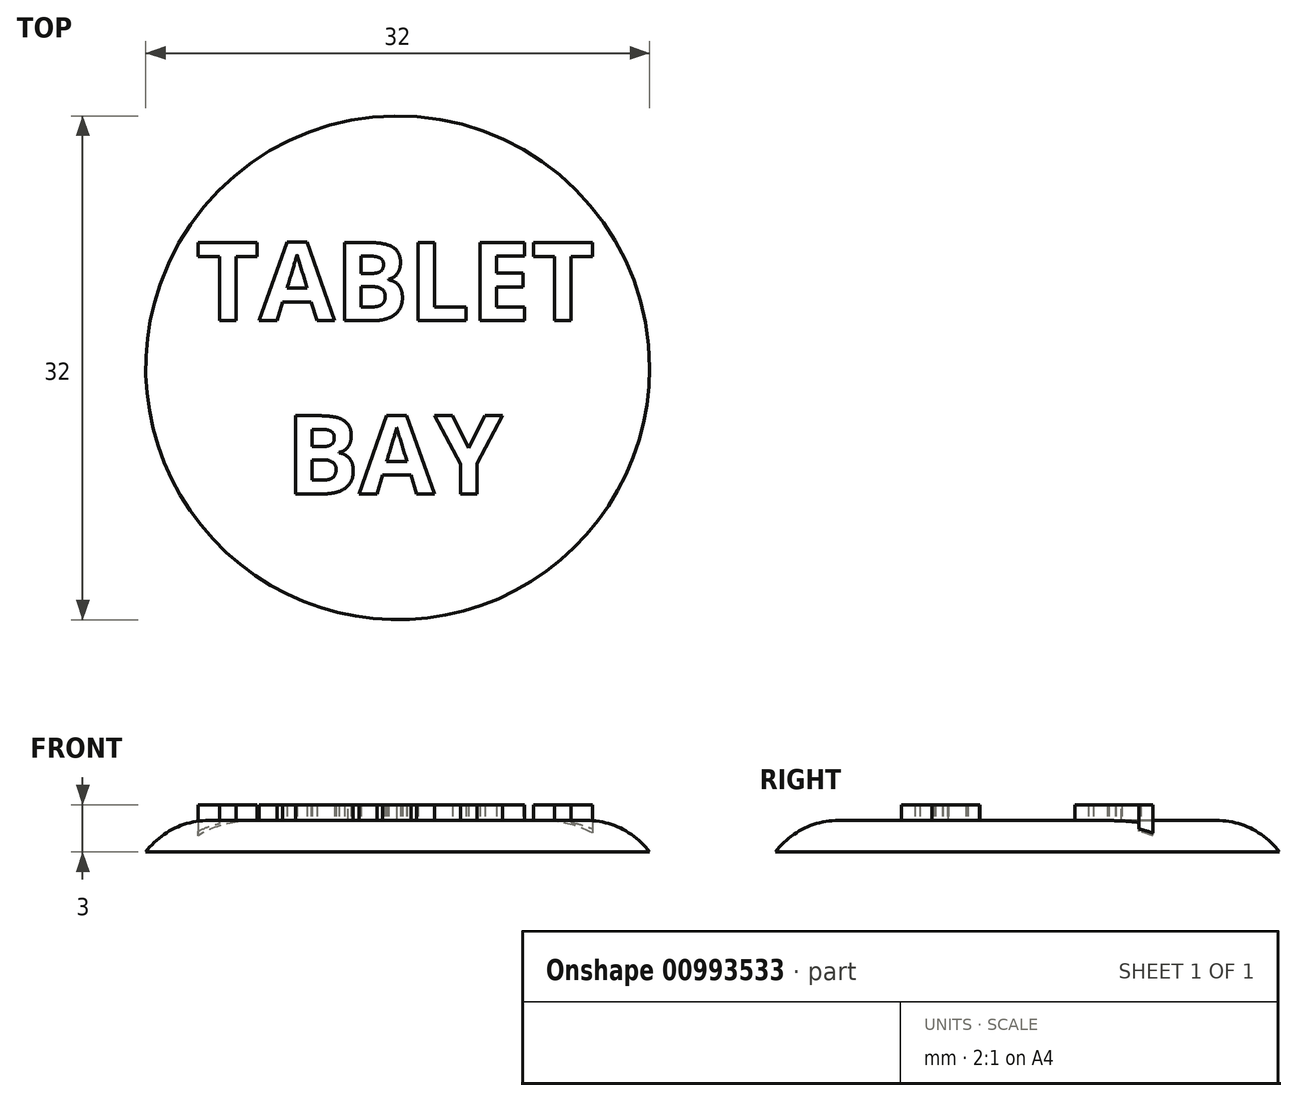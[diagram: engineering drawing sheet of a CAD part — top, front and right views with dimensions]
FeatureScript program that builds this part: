
annotation { "Feature Type Name" : "Feature", "Feature Type Description" : "" }
export const myFeature = defineFeature(function(context is Context, id is Id, definition is map)
    precondition{}
    {
        {
            var Q0;
            Q0=qCreatedBy(makeId("Top.planeOp"),FACE);
            var sketch = newSketch(context, id + "F0", { "sketchPlane" : qUnion([Q0])});
            skCircle(sketch, "E0", {"center": v(0, 0) * mm, "radius": 16 * mm});
            skSolve(sketch);
        }
        {
            var Q0;
            Q0=qSketchRegion(id+"F0",true);
            extrude(context, id + "F1", {"entities" : qUnion([Q0]), "depth" : 2 * mm, "offsetDistance" : 25 * mm});
        }
        {
            var Q0;
            Q0=makeQuery(id+"F1.opExtrude","CAP_EDGE",EDGE,{"disambiguationData":[OSD([sQuery(id+"F0.wireOp",EDGE,"E0")])],"isStart":false});
            fillet(context, id + "F2", {"entities" : qUnion([Q0]), "radius" : 5 * mm, "tangentPropagation" : true, "allowEdgeOverflow" : false});
        }
        {
            var Q0;
            Q0=makeQuery(id+"F1.opExtrude","CAP_FACE",FACE,{"disambiguationData":[OSD([sQuery(id+"F0.wireOp",EDGE,"E0")])],"isStart":false});
            var sketch = newSketch(context, id + "F3", { "sketchPlane" : qUnion([Q0])});
            skText(sketch, "E1", { "text": "TABLET", "fontName": "OpenSans-Bold.ttf"});
            skText(sketch, "E2", { "text": "BAY", "fontName": "OpenSans-Bold.ttf"});
            skLineSegment(sketch, "E3", {"start": v(0, -3) * mm, "end": v(0, 0) * mm, "construction": true});
            skLineSegment(sketch, "E4", {"start": v(0, 0) * mm, "end": v(0, 3) * mm, "construction": true});
            const initialGuessF3  = {"E1": [-0.01281, 0.003, 1, 0, 0.005], "E2": [-0.00712, -0.008, 1, 0, 0.005]};
            skSetInitialGuess(sketch, initialGuessF3);
            skSolve(sketch);
        }
        {
            var Q0;
            Q0=qSketchRegion(id+"F3",true);
            extrude(context, id + "F4", {"entities" : qUnion([Q0]), "operationType" : NewBodyOperationType.ADD, "depth" : 1 * mm, "offsetDistance" : 25 * mm, "hasSecondDirection" : true, "secondDirectionOppositeDirection" : true, "secondDirectionDepth" : 1 * mm});
        }
    });
